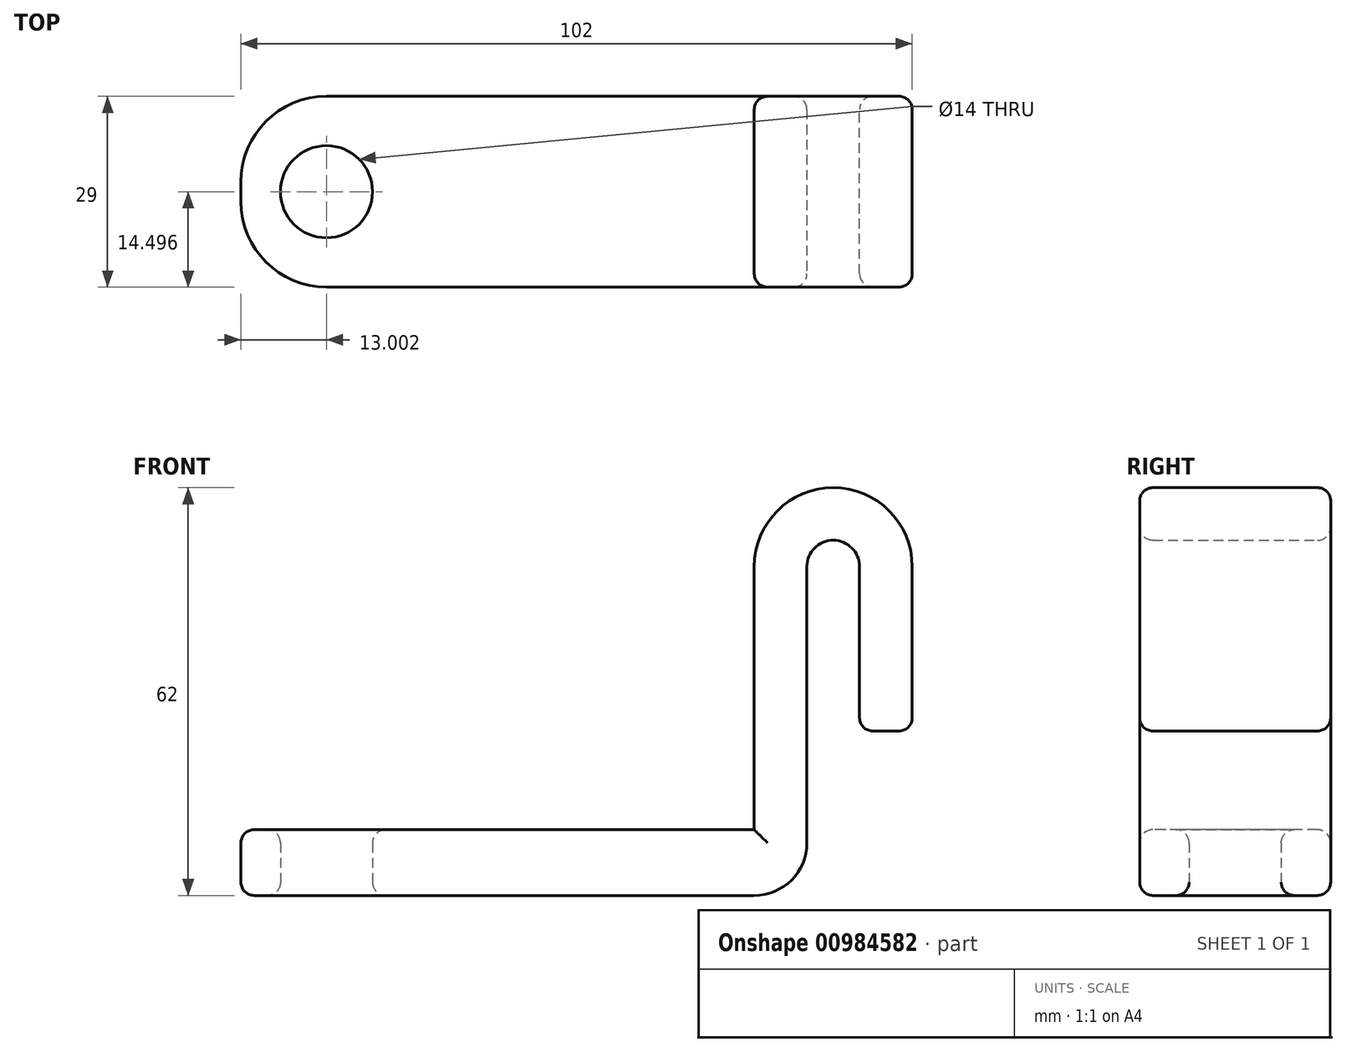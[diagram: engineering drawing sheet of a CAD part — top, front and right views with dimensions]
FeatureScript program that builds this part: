
annotation { "Feature Type Name" : "Feature", "Feature Type Description" : "" }
export const myFeature = defineFeature(function(context is Context, id is Id, definition is map)
    precondition{}
    {
        {
            var Q0;
            Q0=qCreatedBy(makeId("Top.planeOp"),FACE);
            var sketch = newSketch(context, id + "F0", { "sketchPlane" : qUnion([Q0])});
            skLineSegment(sketch, "E0.top", {"start": v(-59.34, -15.7) * mm, "end": v(13.66, -15.7) * mm});
            skLineSegment(sketch, "E0.left", {"start": v(-72.34, 0.3) * mm, "end": v(-72.34, -2.7) * mm});
            skLineSegment(sketch, "E0.right", {"start": v(13.66, 13.3) * mm, "end": v(13.66, -15.7) * mm});
            skPoint(sketch, "E1.visualSharp", {"position": v(-72.34, 13.3) * mm});
            skPoint(sketch, "E2.visualSharp", {"position": v(-72.34, -15.7) * mm});
            skArc(sketch, "E2.filletArc", {"start": v(-72.34, -2.7) * mm, "mid": v(-68.53, -11.89) * mm, "end": v(-59.34, -15.7) * mm});
            skArc(sketch, "E3.MirrorCS", {"start": v(-72.34, 0.3) * mm, "mid": v(-68.53, 9.5) * mm, "end": v(-59.34, 13.3) * mm});
            skLineSegment(sketch, "E4", {"start": v(-59.34, 13.3) * mm, "end": v(13.66, 13.3) * mm});
            skCircle(sketch, "E5", {"center": v(-59.34, -1.2) * mm, "radius": 7 * mm});
            skPoint(sketch, "E5.centerSnap0", {"position": v(13.66, -1.2) * mm});
            skSolve(sketch);
        }
        {
            var Q0;
            Q0=makeQuery(id+"F0.imprint","IMPRINT",FACE,{"disambiguationData":[TD([[makeQuery(id+"F0.imprint","IMPRINT",EDGE,{"derivedFrom":sQuery(id+"F0.wireOp",EDGE,"E0.top")}),1.0]])]});
            extrude(context, id + "F1", {"entities" : qUnion([Q0]), "depth" : 10 * mm, "offsetDistance" : 25 * mm});
        }
        {
            var Q0;
            Q0=makeQuery(id+"F1.opExtrude","SWEPT_FACE",FACE,{"disambiguationData":[OSD([sQuery(id+"F0.wireOp",EDGE,"E0.right")])]});
            var sketch = newSketch(context, id + "F2", { "sketchPlane" : qUnion([Q0])});
            skLineSegment(sketch, "E6.top", {"start": v(-15.7, 50) * mm, "end": v(-15.7, 50) * mm});
            skLineSegment(sketch, "E6.left", {"start": v(-15.7, 10) * mm, "end": v(-15.7, 50) * mm});
            skLineSegment(sketch, "E6.right", {"start": v(-15.7, 15.99) * mm, "end": v(-15.7, 50) * mm});
            skLineSegment(sketch, "E7.bottom", {"start": v(13.3, 10) * mm, "end": v(-15.7, 10) * mm});
            skLineSegment(sketch, "E7.top", {"start": v(13.3, 50) * mm, "end": v(-15.7, 50) * mm});
            skLineSegment(sketch, "E7.left", {"start": v(13.3, 10) * mm, "end": v(13.3, 50) * mm});
            skSolve(sketch);
        }
        {
            var Q0;
            Q0 = qSketchRegion(id + "F2", true);
            extrude(context, id + "F3", {"entities" : qUnion([Q0]), "operationType" : NewBodyOperationType.ADD, "oppositeDirection" : true, "depth" : 8 * mm, "offsetDistance" : 25 * mm});
        }
        {
            var Q0;
            Q0=makeQuery(id+"F3.boolean.opBoolean","MERGE",FACE,{"derivedFrom":[makeQuery(id+"F1.opExtrude","SWEPT_FACE",FACE,{"disambiguationData":[OSD([sQuery(id+"F0.wireOp",EDGE,"E4")])]}),makeQuery(id+"F3.opExtrude","SWEPT_FACE",FACE,{"disambiguationData":[OSD([sQuery(id+"F2.wireOp",EDGE,"E7.left")])]})]});
            var sketch = newSketch(context, id + "F4", { "sketchPlane" : qUnion([Q0])});
            skLineSegment(sketch, "E8.0", {"start": v(-13.66, 50) * mm, "end": v(-13.66, 0) * mm});
            skArc(sketch, "E9", {"start": v(-13.66, 50) * mm, "mid": v(-17.66, 54) * mm, "end": v(-21.66, 50) * mm});
            skLineSegment(sketch, "E10", {"start": v(-21.66, 50) * mm, "end": v(-21.66, 25) * mm});
            skPoint(sketch, "E10.endSnap0", {"position": v(-13.66, 25) * mm});
            skSolve(sketch);
        }
        {
            var Q0;
            Q0=makeQuery(id+"F3.opExtrude","SWEPT_FACE",FACE,{"disambiguationData":[OSD([sQuery(id+"F2.wireOp",EDGE,"E7.top")])]});
            var Q1;
            Q1=sQuery(id+"F4.wireOp",EDGE,"E9");
            var Q2;
            Q2=sQuery(id+"F4.wireOp",EDGE,"E10");
            sweep(context, id + "F5", {"operationType" : NewBodyOperationType.ADD, "profiles" : qUnion([Q0]), "path" : qUnion([Q1, Q2])});
        }
        {
            var Q0;
            {var subQ0=sQuery(id+"F2.wireOp",EDGE,"E7.left");Q0=makeQuery(id+"F5.boolean.opBoolean","MERGE",FACE,{"derivedFrom":[makeQuery(id+"F3.boolean.opBoolean","MERGE",FACE,{"derivedFrom":[makeQuery(id+"F1.opExtrude","SWEPT_FACE",FACE,{"disambiguationData":[OSD([sQuery(id+"F0.wireOp",EDGE,"E4")])]}),makeQuery(id+"F3.opExtrude","SWEPT_FACE",FACE,{"disambiguationData":[OSD([subQ0])]})]}),makeQuery(id+"F5.opSweep","SWEPT_FACE",FACE,{"disambiguationData":[OSD([sQuery(id+"F2.wireOp",EDGE,"E7.top"),subQ0,sQuery(id+"F4.wireOp",EDGE,"E9")])]})]});}
            var Q1;
            {var subQ0=sQuery(id+"F2.wireOp",EDGE,"E6.left");Q1=makeQuery(id+"F5.boolean.opBoolean","MERGE",FACE,{"derivedFrom":[makeQuery(id+"F3.boolean.opBoolean","MERGE",FACE,{"derivedFrom":[makeQuery(id+"F1.opExtrude","SWEPT_FACE",FACE,{"disambiguationData":[OSD([sQuery(id+"F0.wireOp",EDGE,"E0.top")])]}),makeQuery(id+"F3.opExtrude","SWEPT_FACE",FACE,{"disambiguationData":[OSD([subQ0])]})]}),makeQuery(id+"F5.opSweep","SWEPT_FACE",FACE,{"disambiguationData":[OSD([sQuery(id+"F2.wireOp",EDGE,"E7.top"),subQ0,sQuery(id+"F4.wireOp",EDGE,"E9")])]})]});}
            var Q2;
            Q2=makeQuery(id+"F5.opSweep","CAP_FACE",FACE,{"disambiguationData":[OSD([sQuery(id+"F2.wireOp",EDGE,"E7.top"),sQuery(id+"F4.wireOp",VERTEX,"E10.end")])],"isStart":false});
            var Q3;
            Q3=makeQuery(id+"F1.opExtrude","CAP_EDGE",EDGE,{"disambiguationData":[OSD([sQuery(id+"F0.wireOp",EDGE,"E5")])],"isStart":false});
            var Q4;
            Q4=makeQuery(id+"F1.opExtrude","CAP_EDGE",EDGE,{"disambiguationData":[OSD([sQuery(id+"F0.wireOp",EDGE,"E5")])],"isStart":true});
            fillet(context, id + "F6", {"entities" : qUnion([Q0, Q1, Q2, Q3, Q4]), "radius" : 2 * mm, "tangentPropagation" : true, "allowEdgeOverflow" : false});
        }
        {
            var Q0;
            Q0=makeQuery(id+"F1.opExtrude","CAP_EDGE",EDGE,{"disambiguationData":[OSD([sQuery(id+"F0.wireOp",EDGE,"E0.right")])],"isStart":true});
            var Q1;
            Q1=makeQuery(id+"F3.opExtrude","CAP_EDGE",EDGE,{"disambiguationData":[OSD([sQuery(id+"F2.wireOp",EDGE,"E7.bottom")])],"isStart":false});
            fillet(context, id + "F7", {"entities" : qUnion([Q0, Q1]), "radius" : 8 * mm, "tangentPropagation" : true, "allowEdgeOverflow" : false});
        }
    });
